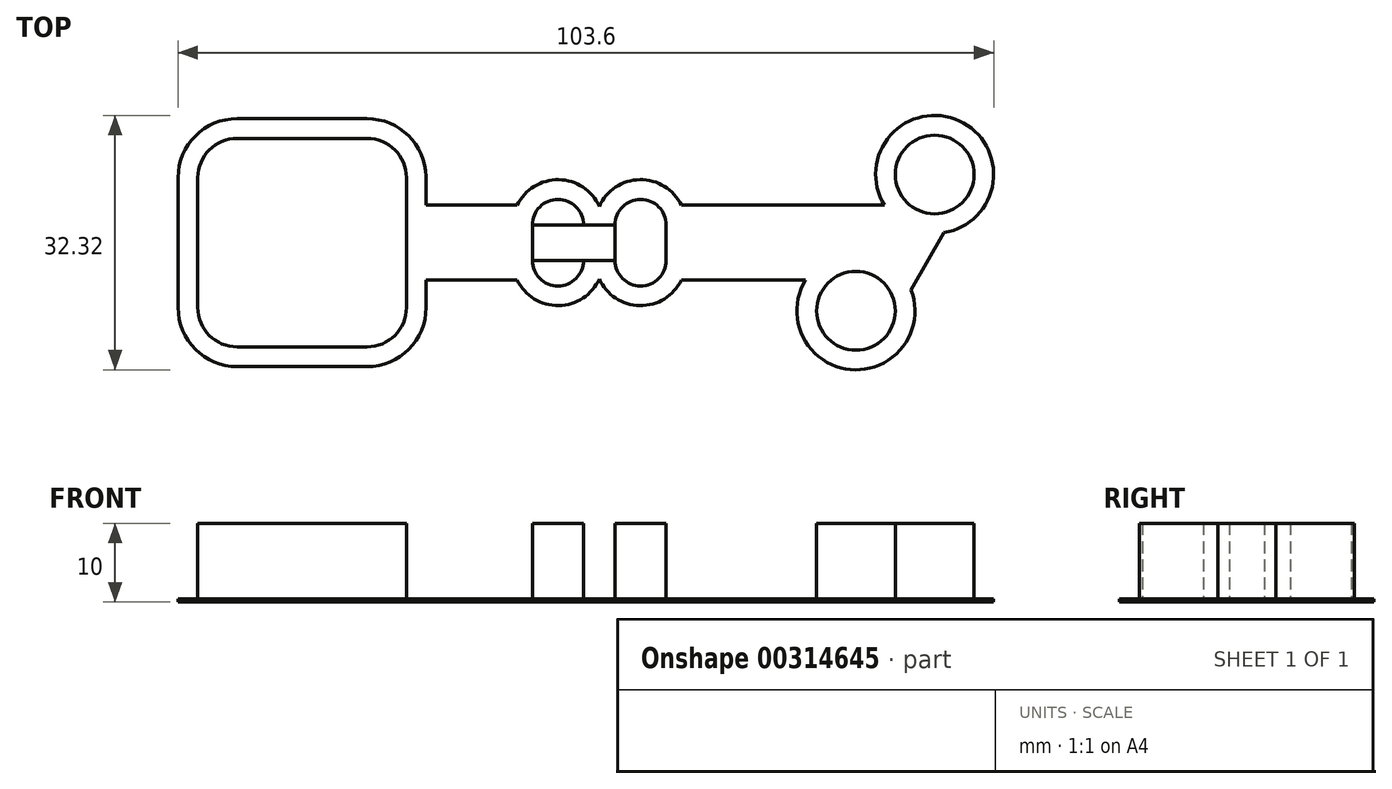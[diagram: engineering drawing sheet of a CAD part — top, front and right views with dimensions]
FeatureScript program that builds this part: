
annotation { "Feature Type Name" : "Feature", "Feature Type Description" : "" }
export const myFeature = defineFeature(function(context is Context, id is Id, definition is map)
    precondition{}
    {
        {
            var Q0;
            Q0=qCreatedBy(makeId("Top.planeOp"),FACE);
            var sketch = newSketch(context, id + "F0", { "sketchPlane" : qUnion([Q0])});
            skLineSegment(sketch, "E0.bottom", {"start": v(-8.25, 13.25) * mm, "end": v(8.25, 13.25) * mm});
            skLineSegment(sketch, "E0.top", {"start": v(-8.25, -13.25) * mm, "end": v(8.25, -13.25) * mm});
            skLineSegment(sketch, "E0.left", {"start": v(-13.25, 8.25) * mm, "end": v(-13.25, -8.25) * mm});
            skLineSegment(sketch, "E0.right", {"start": v(13.25, 8.25) * mm, "end": v(13.25, 8.25) * mm});
            skPoint(sketch, "E0.middle", {"position": v(0, 0) * mm});
            skPoint(sketch, "E1.visualSharp", {"position": v(-13.25, 13.25) * mm});
            skArc(sketch, "E1.filletArc", {"start": v(-8.25, 13.25) * mm, "mid": v(-11.79, 11.79) * mm, "end": v(-13.25, 8.25) * mm});
            skPoint(sketch, "E2.visualSharp", {"position": v(-13.25, -13.25) * mm});
            skArc(sketch, "E2.filletArc", {"start": v(-13.25, -8.25) * mm, "mid": v(-11.79, -11.79) * mm, "end": v(-8.25, -13.25) * mm});
            skPoint(sketch, "E3.visualSharp", {"position": v(13.25, -13.25) * mm});
            skArc(sketch, "E3.filletArc", {"start": v(8.25, -13.25) * mm, "mid": v(11.79, -11.79) * mm, "end": v(13.25, -8.25) * mm});
            skPoint(sketch, "E4.visualSharp", {"position": v(13.25, 13.25) * mm});
            skCircle(sketch, "E5", {"center": v(0, 0) * mm, "radius": 4.5 * mm});
            skLineSegment(sketch, "E6", {"start": v(-4.5, 13.25) * mm, "end": v(-4.5, -13.25) * mm});
            skLineSegment(sketch, "E7", {"start": v(4.5, 13.25) * mm, "end": v(4.5, -13.25) * mm});
            skLineSegment(sketch, "E8", {"start": v(-13.25, 4.5) * mm, "end": v(13.25, 4.5) * mm});
            skLineSegment(sketch, "E9", {"start": v(-13.25, -4.5) * mm, "end": v(13.25, -4.5) * mm});
            skLineSegment(sketch, "E10", {"start": v(-32.84, 0) * mm, "end": v(112.9, 0) * mm, "construction": true});
            skPoint(sketch, "E10.endSnap0", {"position": v(13.25, 0) * mm});
            skLineSegment(sketch, "E11", {"start": v(13.25, 2.25) * mm, "end": v(13.25, 2.25) * mm});
            skLineSegment(sketch, "E12", {"start": v(29.25, 2.25) * mm, "end": v(29.25, 0) * mm});
            skLineSegment(sketch, "E13.bottom", {"start": v(29.25, 2.25) * mm, "end": v(35.75, 2.25) * mm});
            skLineSegment(sketch, "E13.top", {"start": v(29.25, -2.25) * mm, "end": v(35.75, -2.25) * mm});
            skLineSegment(sketch, "E13.left", {"start": v(29.25, 2.25) * mm, "end": v(29.25, -2.25) * mm});
            skLineSegment(sketch, "E13.right", {"start": v(35.75, 2.25) * mm, "end": v(35.75, -2.25) * mm});
            skLineSegment(sketch, "E14", {"start": v(35.75, 0) * mm, "end": v(37.75, 0) * mm, "construction": true});
            skLineSegment(sketch, "E15", {"start": v(37.75, 0) * mm, "end": v(37.75, 13.18) * mm, "construction": true});
            skLineSegment(sketch, "E16.MirrorCS", {"start": v(13.25, -2.25) * mm, "end": v(29.25, -2.25) * mm});
            skLineSegment(sketch, "E17.MirrorCS", {"start": v(37.75, 0) * mm, "end": v(37.75, -13.18) * mm, "construction": true});
            skLineSegment(sketch, "E18.MirrorCS", {"start": v(29.25, -2.25) * mm, "end": v(29.25, 2.25) * mm});
            skLineSegment(sketch, "E19.MirrorCS", {"start": v(35.75, -2.25) * mm, "end": v(35.75, 2.25) * mm});
            skLineSegment(sketch, "E20.MirrorCS", {"start": v(39.75, 2.25) * mm, "end": v(39.75, -2.25) * mm});
            skLineSegment(sketch, "E21.MirrorCS", {"start": v(46.25, 2.25) * mm, "end": v(46.25, -2.25) * mm});
            skLineSegment(sketch, "E22.MirrorCS", {"start": v(46.25, -2.25) * mm, "end": v(39.75, -2.25) * mm});
            skLineSegment(sketch, "E23.MirrorCS", {"start": v(46.25, 2.25) * mm, "end": v(39.75, 2.25) * mm});
            skLineSegment(sketch, "E24", {"start": v(35.75, -2.25) * mm, "end": v(39.75, -2.25) * mm});
            skLineSegment(sketch, "E25", {"start": v(35.75, 2.25) * mm, "end": v(39.75, 2.25) * mm});
            skArc(sketch, "E26", {"start": v(29.25, 2.25) * mm, "mid": v(32.5, 5.5) * mm, "end": v(35.75, 2.25) * mm});
            skArc(sketch, "E27.MirrorCS", {"start": v(46.25, 2.25) * mm, "mid": v(43, 5.5) * mm, "end": v(39.75, 2.25) * mm});
            skArc(sketch, "E28.MirrorCS", {"start": v(29.25, -2.25) * mm, "mid": v(32.5, -5.5) * mm, "end": v(35.75, -2.25) * mm});
            skArc(sketch, "E29.MirrorCS", {"start": v(46.25, -2.25) * mm, "mid": v(43, -5.5) * mm, "end": v(39.75, -2.25) * mm});
            skLineSegment(sketch, "E30", {"start": v(46.25, 2.25) * mm, "end": v(72.75, 2.25) * mm});
            skLineSegment(sketch, "E31", {"start": v(80.35, 8.66) * mm, "end": v(70.35, -8.66) * mm, "construction": true});
            skPoint(sketch, "E32", {"position": v(75.35, 0) * mm});
            skLineSegment(sketch, "E33", {"start": v(76.17, 5.92) * mm, "end": v(74.05, 2.25) * mm});
            skLineSegment(sketch, "E34.MirrorCS", {"start": v(80.06, 3.67) * mm, "end": v(74.53, -5.92) * mm});
            skPoint(sketch, "E35", {"position": v(72.75, 0) * mm});
            skLineSegment(sketch, "E36", {"start": v(71.45, -2.25) * mm, "end": v(46.25, -2.25) * mm});
            skLineSegment(sketch, "E37", {"start": v(74.05, 2.25) * mm, "end": v(72.75, 2.25) * mm});
            skLineSegment(sketch, "E38", {"start": v(13.25, -2.25) * mm, "end": v(13.25, -8.25) * mm});
            skLineSegment(sketch, "E39", {"start": v(13.25, 4.5) * mm, "end": v(13.25, 4.5) * mm});
            skLineSegment(sketch, "E40", {"start": v(13.25, 2.25) * mm, "end": v(29.25, 2.25) * mm});
            skLineSegment(sketch, "E41", {"start": v(13.25, 2.25) * mm, "end": v(13.25, 0) * mm});
            skLineSegment(sketch, "E42", {"start": v(13.25, -2.25) * mm, "end": v(13.25, -2.25) * mm});
            skLineSegment(sketch, "E43", {"start": v(13.25, 0) * mm, "end": v(13.25, -2.25) * mm});
            skLineSegment(sketch, "E44", {"start": v(13.25, 4.5) * mm, "end": v(13.25, 2.25) * mm});
            skLineSegment(sketch, "E45", {"start": v(13.25, 8.25) * mm, "end": v(13.25, 8.24) * mm});
            skLineSegment(sketch, "E46", {"start": v(13.25, 8.34) * mm, "end": v(13.25, 8.34) * mm});
            skLineSegment(sketch, "E47", {"start": v(13.25, 8.2) * mm, "end": v(13.25, 8.2) * mm});
            skLineSegment(sketch, "E48", {"start": v(13.25, 8.23) * mm, "end": v(13.25, 8.2) * mm});
            skLineSegment(sketch, "E49", {"start": v(13.25, 8.24) * mm, "end": v(13.25, 8.23) * mm});
            skLineSegment(sketch, "E50", {"start": v(13.25, 8.24) * mm, "end": v(13.25, 8.24) * mm});
            skLineSegment(sketch, "E51", {"start": v(13.25, 8.2) * mm, "end": v(13.25, 4.5) * mm});
            skLineSegment(sketch, "E52", {"start": v(74.05, 2.25) * mm, "end": v(71.45, -2.25) * mm});
            skLineSegment(sketch, "E53", {"start": v(71.45, -2.25) * mm, "end": v(70.63, -3.67) * mm});
            skArc(sketch, "E54", {"start": v(70.63, -3.67) * mm, "mid": v(67.85, -13) * mm, "end": v(74.53, -5.92) * mm});
            skArc(sketch, "E55", {"start": v(74.53, -5.92) * mm, "mid": v(72.85, -4.33) * mm, "end": v(70.63, -3.67) * mm});
            skArc(sketch, "E56", {"start": v(76.17, 5.92) * mm, "mid": v(77.85, 4.33) * mm, "end": v(80.06, 3.67) * mm});
            skArc(sketch, "E57", {"start": v(80.06, 3.67) * mm, "mid": v(82.85, 13) * mm, "end": v(76.17, 5.92) * mm});
            skLineSegment(sketch, "E58.0", {"start": v(-8.25, 15.75) * mm, "end": v(8.25, 15.75) * mm});
            skArc(sketch, "E58.1", {"start": v(-8.25, 15.75) * mm, "mid": v(-13.55, 13.55) * mm, "end": v(-15.75, 8.25) * mm});
            skLineSegment(sketch, "E58.2", {"start": v(-15.75, 8.25) * mm, "end": v(-15.75, -8.25) * mm});
            skArc(sketch, "E58.3", {"start": v(-15.75, -8.25) * mm, "mid": v(-13.55, -13.55) * mm, "end": v(-8.25, -15.75) * mm});
            skLineSegment(sketch, "E58.4", {"start": v(-8.25, -15.75) * mm, "end": v(8.25, -15.75) * mm});
            skArc(sketch, "E58.5", {"start": v(8.25, -15.75) * mm, "mid": v(13.55, -13.55) * mm, "end": v(15.75, -8.25) * mm});
            skLineSegment(sketch, "E58.6", {"start": v(15.75, -4.75) * mm, "end": v(15.75, -8.25) * mm});
            skLineSegment(sketch, "E58.7", {"start": v(15.75, -4.75) * mm, "end": v(27.32, -4.75) * mm});
            skArc(sketch, "E58.8", {"start": v(27.32, -4.75) * mm, "mid": v(32.59, -8) * mm, "end": v(37.75, -4.6) * mm});
            skArc(sketch, "E58.9", {"start": v(48.18, 4.75) * mm, "mid": v(42.91, 8) * mm, "end": v(37.75, 4.6) * mm});
            skArc(sketch, "E58.10", {"start": v(27.32, 4.75) * mm, "mid": v(32.59, 8) * mm, "end": v(37.75, 4.6) * mm});
            skLineSegment(sketch, "E58.11", {"start": v(15.75, 4.75) * mm, "end": v(27.32, 4.75) * mm});
            skLineSegment(sketch, "E58.12", {"start": v(15.75, 8.2) * mm, "end": v(15.75, 4.75) * mm});
            skLineSegment(sketch, "E58.13", {"start": v(48.18, 4.75) * mm, "end": v(73.95, 4.75) * mm});
            skArc(sketch, "E58.14", {"start": v(81.56, 1.26) * mm, "mid": v(83.47, 15.48) * mm, "end": v(73.95, 4.75) * mm});
            skLineSegment(sketch, "E58.15", {"start": v(81.56, 1.26) * mm, "end": v(77.36, -6) * mm});
            skArc(sketch, "E58.16", {"start": v(63.95, -4.75) * mm, "mid": v(69.65, -16.13) * mm, "end": v(77.36, -6) * mm});
            skLineSegment(sketch, "E58.17", {"start": v(63.95, -4.75) * mm, "end": v(48.18, -4.75) * mm});
            skArc(sketch, "E58.18", {"start": v(48.18, -4.75) * mm, "mid": v(42.91, -8) * mm, "end": v(37.75, -4.6) * mm});
            skArc(sketch, "E59.0", {"start": v(15.75, 8.38) * mm, "mid": v(13.5, 13.6) * mm, "end": v(8.25, 15.75) * mm});
            skLineSegment(sketch, "E60", {"start": v(15.75, 8.2) * mm, "end": v(15.75, 8.38) * mm});
            skArc(sketch, "E61", {"start": v(13.25, 8.34) * mm, "mid": v(11.75, 11.82) * mm, "end": v(8.25, 13.25) * mm});
            skArc(sketch, "E62", {"start": v(13.25, 8.25) * mm, "mid": v(13.25, 8.3) * mm, "end": v(13.25, 8.34) * mm});
            skSolve(sketch);
        }
        {
            var Q0;
            Q0=makeQuery(id+"F0.imprint","IMPRINT",FACE,{"disambiguationData":[TD([[makeQuery(id+"F0.imprint","IMPRINT",EDGE,{"derivedFrom":sQuery(id+"F0.wireOp",EDGE,"E13.bottom")}),1.0]])]});
            var Q1;
            Q1=makeQuery(id+"F0.imprint","IMPRINT",FACE,{"disambiguationData":[TD([[makeQuery(id+"F0.imprint","IMPRINT",EDGE,{"derivedFrom":sQuery(id+"F0.wireOp",EDGE,"E13.top")}),-1.0]])]});
            var Q2;
            Q2=makeQuery(id+"F0.imprint","IMPRINT",FACE,{"disambiguationData":[TD([[makeQuery(id+"F0.imprint","IMPRINT",EDGE,{"derivedFrom":sQuery(id+"F0.wireOp",EDGE,"E22.MirrorCS")}),1.0]])]});
            var Q3;
            Q3=makeQuery(id+"F0.imprint","IMPRINT",FACE,{"disambiguationData":[TD([[makeQuery(id+"F0.imprint","IMPRINT",EDGE,{"derivedFrom":sQuery(id+"F0.wireOp",EDGE,"E23.MirrorCS")}),-1.0]])]});
            var Q4;
            Q4=makeQuery(id+"F0.imprint","IMPRINT",FACE,{"disambiguationData":[TD([[makeQuery(id+"F0.imprint","IMPRINT",EDGE,{"derivedFrom":sQuery(id+"F0.wireOp",EDGE,"E54")}),1.0]])]});
            var Q5;
            Q5=makeQuery(id+"F0.imprint","IMPRINT",FACE,{"disambiguationData":[TD([[makeQuery(id+"F0.imprint","IMPRINT",EDGE,{"derivedFrom":sQuery(id+"F0.wireOp",EDGE,"E56")}),1.0]])]});
            var Q6;
            {var subQ0=sQuery(id+"F0.wireOp",EDGE,"E1.filletArc");Q6=makeQuery(id+"F0.imprint","IMPRINT",FACE,{"disambiguationData":[TD([[makeQuery(id+"F0.imprint","IMPRINT",EDGE,{"derivedFrom":subQ0}),1.0]])]});}
            var Q7;
            Q7=makeQuery(id+"F0.imprint","IMPRINT",FACE,{"disambiguationData":[TD([[makeQuery(id+"F0.imprint","IMPRINT",EDGE,{"derivedFrom":sQuery(id+"F0.wireOp",EDGE,"E45")}),-1.0]])]});
            var Q8;
            {var subQ5=sQuery(id+"F0.wireOp",EDGE,"E2.filletArc");Q8=makeQuery(id+"F0.imprint","IMPRINT",FACE,{"disambiguationData":[TD([[makeQuery(id+"F0.imprint","IMPRINT",EDGE,{"derivedFrom":subQ5}),1.0]])]});}
            var Q9;
            {var subQ7=sQuery(id+"F0.wireOp",EDGE,"E3.filletArc");Q9=makeQuery(id+"F0.imprint","IMPRINT",FACE,{"disambiguationData":[TD([[makeQuery(id+"F0.imprint","IMPRINT",EDGE,{"derivedFrom":subQ7}),1.0]])]});}
            var Q10;
            {var subQ2=sQuery(id+"F0.wireOp",EDGE,"E6");var subQ5=sQuery(id+"F0.wireOp",EDGE,"E0.bottom");var subQ8=makeQuery(id+"F0.imprint","INTERSECT",VERTEX,{"derivedFrom":[subQ5,subQ2]});Q10=makeQuery(id+"F0.imprint","IMPRINT",FACE,{"disambiguationData":[TD([[makeQuery(id+"F0.imprint","IMPRINT",EDGE,{"disambiguationData":[TD([[subQ8,-1.0]])],"derivedFrom":subQ5}),-1.0]])]});}
            var Q11;
            {var subQ1=sQuery(id+"F0.wireOp",EDGE,"E0.top");var subQ6=sQuery(id+"F0.wireOp",EDGE,"E6");var subQ8=makeQuery(id+"F0.imprint","INTERSECT",VERTEX,{"derivedFrom":[subQ1,subQ6]});Q11=makeQuery(id+"F0.imprint","IMPRINT",FACE,{"disambiguationData":[TD([[makeQuery(id+"F0.imprint","IMPRINT",EDGE,{"disambiguationData":[TD([[subQ8,-1.0]])],"derivedFrom":subQ1}),1.0]])]});}
            var Q12;
            {var subQ0=sQuery(id+"F0.wireOp",EDGE,"E8");var subQ1=sQuery(id+"F0.wireOp",EDGE,"E0.left");var subQ2=makeQuery(id+"F0.imprint","INTERSECT",VERTEX,{"derivedFrom":[subQ1,subQ0]});Q12=makeQuery(id+"F0.imprint","IMPRINT",FACE,{"disambiguationData":[TD([[makeQuery(id+"F0.imprint","IMPRINT",EDGE,{"disambiguationData":[TD([[subQ2,-1.0]])],"derivedFrom":subQ1}),1.0]])]});}
            var Q13;
            Q13=makeQuery(id+"F0.imprint","IMPRINT",FACE,{"disambiguationData":[TD([[makeQuery(id+"F0.imprint","IMPRINT",EDGE,{"derivedFrom":sQuery(id+"F0.wireOp",EDGE,"E20.MirrorCS")}),1.0]])]});
            var Q14;
            Q14=makeQuery(id+"F0.imprint","IMPRINT",FACE,{"disambiguationData":[TD([[makeQuery(id+"F0.imprint","IMPRINT",EDGE,{"derivedFrom":sQuery(id+"F0.wireOp",EDGE,"E41")}),-1.0]])]});
            var Q15;
            {var subQ0=sQuery(id+"F0.wireOp",EDGE,"E5");var subQ1=makeQuery(id+"F0.imprint","INTERSECT",VERTEX,{"derivedFrom":[subQ0,sQuery(id+"F0.wireOp",EDGE,"E8")]});Q15=makeQuery(id+"F0.imprint","IMPRINT",FACE,{"disambiguationData":[TD([[makeQuery(id+"F0.imprint","IMPRINT",EDGE,{"disambiguationData":[TD([[subQ1,1.0]])],"derivedFrom":subQ0}),1.0]])]});}
            var Q16;
            {var subQ0=sQuery(id+"F0.wireOp",EDGE,"E6");var subQ1=sQuery(id+"F0.wireOp",EDGE,"E5");var subQ2=makeQuery(id+"F0.imprint","INTERSECT",VERTEX,{"derivedFrom":[subQ1,subQ0]});Q16=makeQuery(id+"F0.imprint","IMPRINT",FACE,{"disambiguationData":[TD([[makeQuery(id+"F0.imprint","IMPRINT",EDGE,{"disambiguationData":[TD([[subQ2,-1.0]])],"derivedFrom":subQ1}),-1.0]])]});}
            var Q17;
            {var subQ0=sQuery(id+"F0.wireOp",EDGE,"E8");var subQ1=sQuery(id+"F0.wireOp",EDGE,"E5");var subQ2=makeQuery(id+"F0.imprint","INTERSECT",VERTEX,{"derivedFrom":[subQ1,subQ0]});Q17=makeQuery(id+"F0.imprint","IMPRINT",FACE,{"disambiguationData":[TD([[makeQuery(id+"F0.imprint","IMPRINT",EDGE,{"disambiguationData":[TD([[subQ2,-1.0]])],"derivedFrom":subQ1}),-1.0]])]});}
            var Q18;
            {var subQ0=sQuery(id+"F0.wireOp",EDGE,"E7");var subQ1=sQuery(id+"F0.wireOp",EDGE,"E5");var subQ2=makeQuery(id+"F0.imprint","INTERSECT",VERTEX,{"derivedFrom":[subQ1,subQ0]});Q18=makeQuery(id+"F0.imprint","IMPRINT",FACE,{"disambiguationData":[TD([[makeQuery(id+"F0.imprint","IMPRINT",EDGE,{"disambiguationData":[TD([[subQ2,1.0]])],"derivedFrom":subQ1}),-1.0]])]});}
            var Q19;
            {var subQ0=sQuery(id+"F0.wireOp",EDGE,"E8");var subQ1=sQuery(id+"F0.wireOp",EDGE,"E5");var subQ2=makeQuery(id+"F0.imprint","INTERSECT",VERTEX,{"derivedFrom":[subQ1,subQ0]});Q19=makeQuery(id+"F0.imprint","IMPRINT",FACE,{"disambiguationData":[TD([[makeQuery(id+"F0.imprint","IMPRINT",EDGE,{"disambiguationData":[TD([[subQ2,1.0]])],"derivedFrom":subQ1}),-1.0]])]});}
            var Q20;
            Q20=makeQuery(id+"F0.imprint","IMPRINT",FACE,{"disambiguationData":[TD([[makeQuery(id+"F0.imprint","IMPRINT",EDGE,{"derivedFrom":sQuery(id+"F0.wireOp",EDGE,"E19.MirrorCS")}),1.0]])]});
            var Q21;
            {var subQ2=sQuery(id+"F0.wireOp",EDGE,"E16.MirrorCS");Q21=makeQuery(id+"F0.imprint","IMPRINT",FACE,{"disambiguationData":[TD([[makeQuery(id+"F0.imprint","IMPRINT",EDGE,{"derivedFrom":subQ2}),1.0]])]});}
            var Q22;
            {var subQ0=sQuery(id+"F0.wireOp",EDGE,"E1.filletArc");Q22=makeQuery(id+"F0.imprint","IMPRINT",FACE,{"disambiguationData":[TD([[makeQuery(id+"F0.imprint","IMPRINT",EDGE,{"derivedFrom":subQ0}),-1.0]])]});}
            var Q23;
            Q23=makeQuery(id+"F0.imprint","IMPRINT",FACE,{"disambiguationData":[TD([[makeQuery(id+"F0.imprint","IMPRINT",EDGE,{"derivedFrom":sQuery(id+"F0.wireOp",EDGE,"E19.MirrorCS")}),-1.0]])]});
            var Q24;
            Q24=makeQuery(id+"F0.imprint","IMPRINT",FACE,{"disambiguationData":[TD([[makeQuery(id+"F0.imprint","IMPRINT",EDGE,{"derivedFrom":sQuery(id+"F0.wireOp",EDGE,"E21.MirrorCS")}),1.0]])]});
            var Q25;
            Q25=makeQuery(id+"F0.imprint","IMPRINT",FACE,{"disambiguationData":[TD([[makeQuery(id+"F0.imprint","IMPRINT",EDGE,{"derivedFrom":sQuery(id+"F0.wireOp",EDGE,"E33")}),1.0]])]});
            extrude(context, id + "F1", {"entities" : qUnion([Q0, Q1, Q2, Q3, Q4, Q5, Q6, Q7, Q8, Q9, Q10, Q11, Q12, Q13, Q14, Q15, Q16, Q17, Q18, Q19, Q20, Q21, Q22, Q23, Q24, Q25]), "depth" : 0.4 * mm});
        }
        {
            var Q0;
            {var subQ7=sQuery(id+"F0.wireOp",EDGE,"E3.filletArc");Q0=makeQuery(id+"F0.imprint","IMPRINT",FACE,{"disambiguationData":[TD([[makeQuery(id+"F0.imprint","IMPRINT",EDGE,{"derivedFrom":subQ7}),1.0]])]});}
            var Q1;
            {var subQ1=sQuery(id+"F0.wireOp",EDGE,"E0.top");var subQ6=sQuery(id+"F0.wireOp",EDGE,"E6");var subQ8=makeQuery(id+"F0.imprint","INTERSECT",VERTEX,{"derivedFrom":[subQ1,subQ6]});Q1=makeQuery(id+"F0.imprint","IMPRINT",FACE,{"disambiguationData":[TD([[makeQuery(id+"F0.imprint","IMPRINT",EDGE,{"disambiguationData":[TD([[subQ8,-1.0]])],"derivedFrom":subQ1}),1.0]])]});}
            var Q2;
            {var subQ5=sQuery(id+"F0.wireOp",EDGE,"E2.filletArc");Q2=makeQuery(id+"F0.imprint","IMPRINT",FACE,{"disambiguationData":[TD([[makeQuery(id+"F0.imprint","IMPRINT",EDGE,{"derivedFrom":subQ5}),1.0]])]});}
            var Q3;
            {var subQ0=sQuery(id+"F0.wireOp",EDGE,"E8");var subQ1=sQuery(id+"F0.wireOp",EDGE,"E0.left");var subQ2=makeQuery(id+"F0.imprint","INTERSECT",VERTEX,{"derivedFrom":[subQ1,subQ0]});Q3=makeQuery(id+"F0.imprint","IMPRINT",FACE,{"disambiguationData":[TD([[makeQuery(id+"F0.imprint","IMPRINT",EDGE,{"disambiguationData":[TD([[subQ2,-1.0]])],"derivedFrom":subQ1}),1.0]])]});}
            var Q4;
            {var subQ2=sQuery(id+"F0.wireOp",EDGE,"E6");var subQ5=sQuery(id+"F0.wireOp",EDGE,"E0.bottom");var subQ8=makeQuery(id+"F0.imprint","INTERSECT",VERTEX,{"derivedFrom":[subQ5,subQ2]});Q4=makeQuery(id+"F0.imprint","IMPRINT",FACE,{"disambiguationData":[TD([[makeQuery(id+"F0.imprint","IMPRINT",EDGE,{"disambiguationData":[TD([[subQ8,-1.0]])],"derivedFrom":subQ5}),-1.0]])]});}
            var Q5;
            {var subQ0=sQuery(id+"F0.wireOp",EDGE,"E1.filletArc");Q5=makeQuery(id+"F0.imprint","IMPRINT",FACE,{"disambiguationData":[TD([[makeQuery(id+"F0.imprint","IMPRINT",EDGE,{"derivedFrom":subQ0}),1.0]])]});}
            var Q6;
            Q6=makeQuery(id+"F0.imprint","IMPRINT",FACE,{"disambiguationData":[TD([[makeQuery(id+"F0.imprint","IMPRINT",EDGE,{"derivedFrom":sQuery(id+"F0.wireOp",EDGE,"E45")}),-1.0]])]});
            var Q7;
            Q7=makeQuery(id+"F0.imprint","IMPRINT",FACE,{"disambiguationData":[TD([[makeQuery(id+"F0.imprint","IMPRINT",EDGE,{"derivedFrom":sQuery(id+"F0.wireOp",EDGE,"E41")}),-1.0]])]});
            var Q8;
            {var subQ0=sQuery(id+"F0.wireOp",EDGE,"E8");var subQ1=sQuery(id+"F0.wireOp",EDGE,"E5");var subQ2=makeQuery(id+"F0.imprint","INTERSECT",VERTEX,{"derivedFrom":[subQ1,subQ0]});Q8=makeQuery(id+"F0.imprint","IMPRINT",FACE,{"disambiguationData":[TD([[makeQuery(id+"F0.imprint","IMPRINT",EDGE,{"disambiguationData":[TD([[subQ2,-1.0]])],"derivedFrom":subQ1}),-1.0]])]});}
            var Q9;
            {var subQ0=sQuery(id+"F0.wireOp",EDGE,"E8");var subQ1=sQuery(id+"F0.wireOp",EDGE,"E5");var subQ2=makeQuery(id+"F0.imprint","INTERSECT",VERTEX,{"derivedFrom":[subQ1,subQ0]});Q9=makeQuery(id+"F0.imprint","IMPRINT",FACE,{"disambiguationData":[TD([[makeQuery(id+"F0.imprint","IMPRINT",EDGE,{"disambiguationData":[TD([[subQ2,1.0]])],"derivedFrom":subQ1}),-1.0]])]});}
            var Q10;
            {var subQ0=sQuery(id+"F0.wireOp",EDGE,"E7");var subQ1=sQuery(id+"F0.wireOp",EDGE,"E5");var subQ2=makeQuery(id+"F0.imprint","INTERSECT",VERTEX,{"derivedFrom":[subQ1,subQ0]});Q10=makeQuery(id+"F0.imprint","IMPRINT",FACE,{"disambiguationData":[TD([[makeQuery(id+"F0.imprint","IMPRINT",EDGE,{"disambiguationData":[TD([[subQ2,1.0]])],"derivedFrom":subQ1}),-1.0]])]});}
            var Q11;
            {var subQ0=sQuery(id+"F0.wireOp",EDGE,"E6");var subQ1=sQuery(id+"F0.wireOp",EDGE,"E5");var subQ2=makeQuery(id+"F0.imprint","INTERSECT",VERTEX,{"derivedFrom":[subQ1,subQ0]});Q11=makeQuery(id+"F0.imprint","IMPRINT",FACE,{"disambiguationData":[TD([[makeQuery(id+"F0.imprint","IMPRINT",EDGE,{"disambiguationData":[TD([[subQ2,-1.0]])],"derivedFrom":subQ1}),-1.0]])]});}
            var Q12;
            {var subQ0=sQuery(id+"F0.wireOp",EDGE,"E5");var subQ1=makeQuery(id+"F0.imprint","INTERSECT",VERTEX,{"derivedFrom":[subQ0,sQuery(id+"F0.wireOp",EDGE,"E8")]});Q12=makeQuery(id+"F0.imprint","IMPRINT",FACE,{"disambiguationData":[TD([[makeQuery(id+"F0.imprint","IMPRINT",EDGE,{"disambiguationData":[TD([[subQ1,1.0]])],"derivedFrom":subQ0}),1.0]])]});}
            var Q13;
            Q13=makeQuery(id+"F0.imprint","IMPRINT",FACE,{"disambiguationData":[TD([[makeQuery(id+"F0.imprint","IMPRINT",EDGE,{"derivedFrom":sQuery(id+"F0.wireOp",EDGE,"E13.bottom")}),1.0]])]});
            var Q14;
            Q14=makeQuery(id+"F0.imprint","IMPRINT",FACE,{"disambiguationData":[TD([[makeQuery(id+"F0.imprint","IMPRINT",EDGE,{"derivedFrom":sQuery(id+"F0.wireOp",EDGE,"E19.MirrorCS")}),1.0]])]});
            var Q15;
            Q15=makeQuery(id+"F0.imprint","IMPRINT",FACE,{"disambiguationData":[TD([[makeQuery(id+"F0.imprint","IMPRINT",EDGE,{"derivedFrom":sQuery(id+"F0.wireOp",EDGE,"E13.top")}),-1.0]])]});
            var Q16;
            Q16=makeQuery(id+"F0.imprint","IMPRINT",FACE,{"disambiguationData":[TD([[makeQuery(id+"F0.imprint","IMPRINT",EDGE,{"derivedFrom":sQuery(id+"F0.wireOp",EDGE,"E23.MirrorCS")}),-1.0]])]});
            var Q17;
            Q17=makeQuery(id+"F0.imprint","IMPRINT",FACE,{"disambiguationData":[TD([[makeQuery(id+"F0.imprint","IMPRINT",EDGE,{"derivedFrom":sQuery(id+"F0.wireOp",EDGE,"E20.MirrorCS")}),1.0]])]});
            var Q18;
            Q18=makeQuery(id+"F0.imprint","IMPRINT",FACE,{"disambiguationData":[TD([[makeQuery(id+"F0.imprint","IMPRINT",EDGE,{"derivedFrom":sQuery(id+"F0.wireOp",EDGE,"E22.MirrorCS")}),1.0]])]});
            var Q19;
            Q19=makeQuery(id+"F0.imprint","IMPRINT",FACE,{"disambiguationData":[TD([[makeQuery(id+"F0.imprint","IMPRINT",EDGE,{"derivedFrom":sQuery(id+"F0.wireOp",EDGE,"E56")}),1.0]])]});
            var Q20;
            Q20=makeQuery(id+"F0.imprint","IMPRINT",FACE,{"disambiguationData":[TD([[makeQuery(id+"F0.imprint","IMPRINT",EDGE,{"derivedFrom":sQuery(id+"F0.wireOp",EDGE,"E54")}),1.0]])]});
            extrude(context, id + "F2", {"entities" : qUnion([Q0, Q1, Q2, Q3, Q4, Q5, Q6, Q7, Q8, Q9, Q10, Q11, Q12, Q13, Q14, Q15, Q16, Q17, Q18, Q19, Q20]), "operationType" : NewBodyOperationType.ADD, "depth" : 10 * mm});
        }
    });
